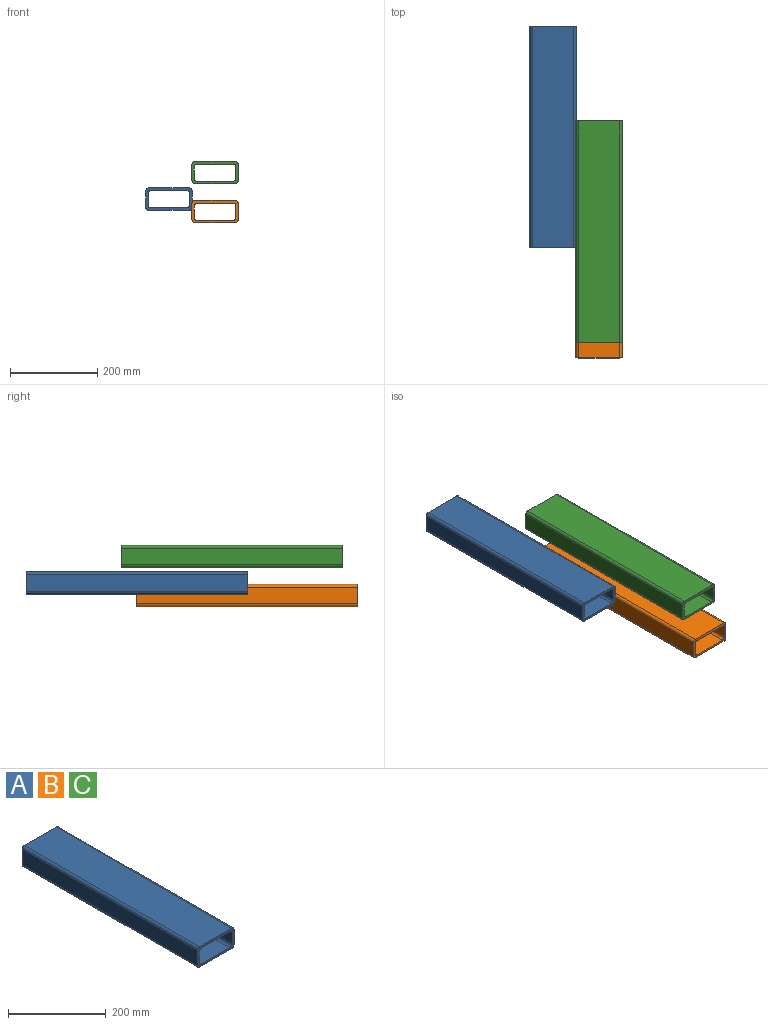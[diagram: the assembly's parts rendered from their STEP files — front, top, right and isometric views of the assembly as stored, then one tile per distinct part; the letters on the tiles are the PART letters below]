
ASSEMBLY  parts=3 mates=2
PART A: 17 faces, bbox 105.9x508x51.1 mm
  f0: plane 508x93.15mm, normal (0,0,-1), area 47322.5mm2, adj f1,f14,f15,f16
  f1: cylinder r=6.35mm len=508mm, axis (0,1,0), area 5067.1mm2, adj f0,f2,f15,f16
  f2: plane 508x38.37mm, normal (1,0,0), area 19492.1mm2, adj f1,f3,f15,f16
  f3: cylinder r=6.35mm len=508mm, axis (0,1,0), area 5067.1mm2, adj f2,f4,f15,f16
  f4: plane 508x93.15mm, normal (0,0,1), area 47322.5mm2, adj f3,f5,f15,f16
  f5: cylinder r=6.35mm len=508mm, axis (0,1,0), area 5067.1mm2, adj f4,f6,f15,f16
  f6: plane 508x38.37mm, normal (-1,0,0), area 19492.1mm2, adj f5,f14,f15,f16
  f7: plane 508x26.92mm, normal (1,0,0), area 13674.4mm2, adj f8,f13,f15,f16
  f8: cylinder r=6.35mm len=508mm, axis (0,1,0), area 5067.1mm2, adj f7,f9,f15,f16
  f9: plane 508x88.36mm, normal (0,0,-1), area 44887.9mm2, adj f8,f10,f15,f16
  f10: plane 508x33.27mm, normal (-1,0,0), area 16900.2mm2, adj f9,f11,f15,f16
  f11: cylinder r=6.35mm len=508mm, axis (0,1,0), area 5067.1mm2, adj f10,f12,f15,f16
  f12: plane 508x82.01mm, normal (0,0,1), area 41662.1mm2, adj f11,f13,f15,f16
  f13: cylinder r=6.35mm len=508mm, axis (0,1,0), area 5067.1mm2, adj f7,f12,f15,f16
  f14: cylinder r=6.35mm len=508mm, axis (0,1,0), area 5067.1mm2, adj f0,f6,f15,f16
  f15: plane 105.85x51.07mm, normal (0,-1,0), area 1645.1mm2, adj f0,f1,f2,f3,f4,f5,f6,f7
  f16: plane 105.85x51.07mm, normal (0,1,0), area 1645.1mm2, adj f0,f1,f2,f3,f4,f5,f6,f7
PART B: same geometry as A
PART C: same geometry as A
PLACE A rot(axis=(0,1,0),180deg) t=(-139.1,250.44,-24.06)mm
PLACE B t=(-33.24,-3.49,-103.71)mm
PLACE C t=(-33.24,32.31,-14.09)mm
MATE planar A.f6 <-> C.f6  axis (1,0,0) through (-86.17,250.44,-49.59)mm
MATE planar B.f6 <-> C.f6  axis (-1,0,0) through (-86.17,-3.49,-78.18)mm
